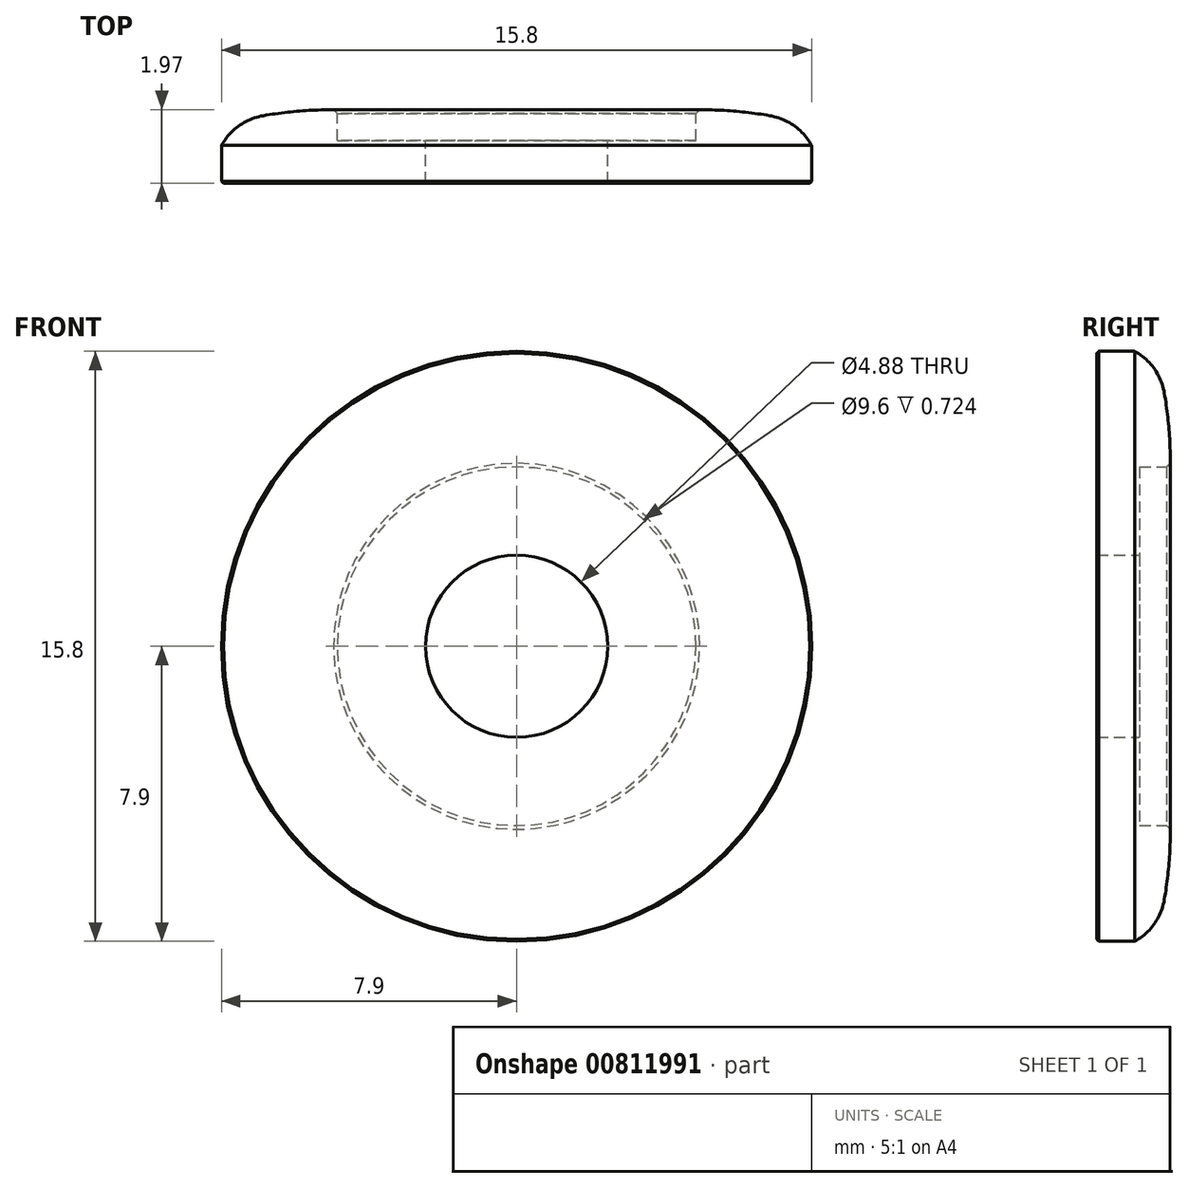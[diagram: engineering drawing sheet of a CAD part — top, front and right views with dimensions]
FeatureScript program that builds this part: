
annotation { "Feature Type Name" : "Feature", "Feature Type Description" : "" }
export const myFeature = defineFeature(function(context is Context, id is Id, definition is map)
    precondition{}
    {
        {
            var Q0;
            Q0=qCreatedBy(makeId("Top.planeOp"),FACE);
            var sketch = newSketch(context, id + "F0", { "sketchPlane" : qUnion([Q0])});
            skLineSegment(sketch, "E0", {"start": v(0, 0) * mm, "end": v(2.44, 0) * mm, "construction": true});
            skLineSegment(sketch, "E1", {"start": v(2.44, 0) * mm, "end": v(7.85, 0) * mm});
            skLineSegment(sketch, "E2", {"start": v(2.44, 0) * mm, "end": v(2.44, 1.14) * mm});
            skLineSegment(sketch, "E3", {"start": v(2.44, 1.14) * mm, "end": v(4.8, 1.14) * mm});
            skLineSegment(sketch, "E4", {"start": v(4.8, 1.14) * mm, "end": v(4.8, 1.87) * mm});
            skLineSegment(sketch, "E5", {"start": v(0, 6.54) * mm, "end": v(0, -9.15) * mm, "construction": true});
            skLineSegment(sketch, "E6", {"start": v(7.9, 0) * mm, "end": v(7.9, 0.05) * mm, "construction": true});
            skLineSegment(sketch, "E7", {"start": v(4.8, 1.87) * mm, "end": v(4.8, 1.87) * mm});
            skLineSegment(sketch, "E8", {"start": v(4.8, 1.87) * mm, "end": v(4.9, 1.97) * mm});
            skArc(sketch, "E9", {"start": v(7.9, 1.02) * mm, "mid": v(7.43, 1.54) * mm, "end": v(6.78, 1.8) * mm});
            skArc(sketch, "E10", {"start": v(4.9, 1.97) * mm, "mid": v(5.84, 1.93) * mm, "end": v(6.78, 1.8) * mm});
            skLineSegment(sketch, "E11", {"start": v(3, 1.97) * mm, "end": v(4.9, 1.97) * mm, "construction": true});
            skLineSegment(sketch, "E12", {"start": v(6.78, 0) * mm, "end": v(6.78, 1.8) * mm, "construction": true});
            skLineSegment(sketch, "E13", {"start": v(4.8, 1.87) * mm, "end": v(4.8, 1.97) * mm, "construction": true});
            skLineSegment(sketch, "E14", {"start": v(4.8, 1.87) * mm, "end": v(4.72, 1.87) * mm, "construction": true});
            skLineSegment(sketch, "E15", {"start": v(2.44, 1.02) * mm, "end": v(7.9, 1.02) * mm, "construction": true});
            skLineSegment(sketch, "E16", {"start": v(7.9, 0.05) * mm, "end": v(7.85, 0) * mm});
            skLineSegment(sketch, "E17", {"start": v(7.9, 0.05) * mm, "end": v(7.9, 1.02) * mm});
            skLineSegment(sketch, "E18", {"start": v(7.85, 0) * mm, "end": v(7.9, 0) * mm, "construction": true});
            skSolve(sketch);
        }
        {
            var Q0;
            Q0=makeQuery(id+"F0.imprint","IMPRINT",FACE,{"disambiguationData":[TD([[makeQuery(id+"F0.imprint","IMPRINT",EDGE,{"derivedFrom":sQuery(id+"F0.wireOp",EDGE,"E1")}),1.0]])]});
            var Q1;
            Q1=sQuery(id+"F0.wireOp",EDGE,"E5");
            revolve(context, id + "F1", {"surfaceOperationType" : NewSurfaceOperationType.NEW, "entities" : qUnion([Q0]), "axis" : qUnion([Q1]), "revolveType" : RevolveType.FULL});
        }
    });
